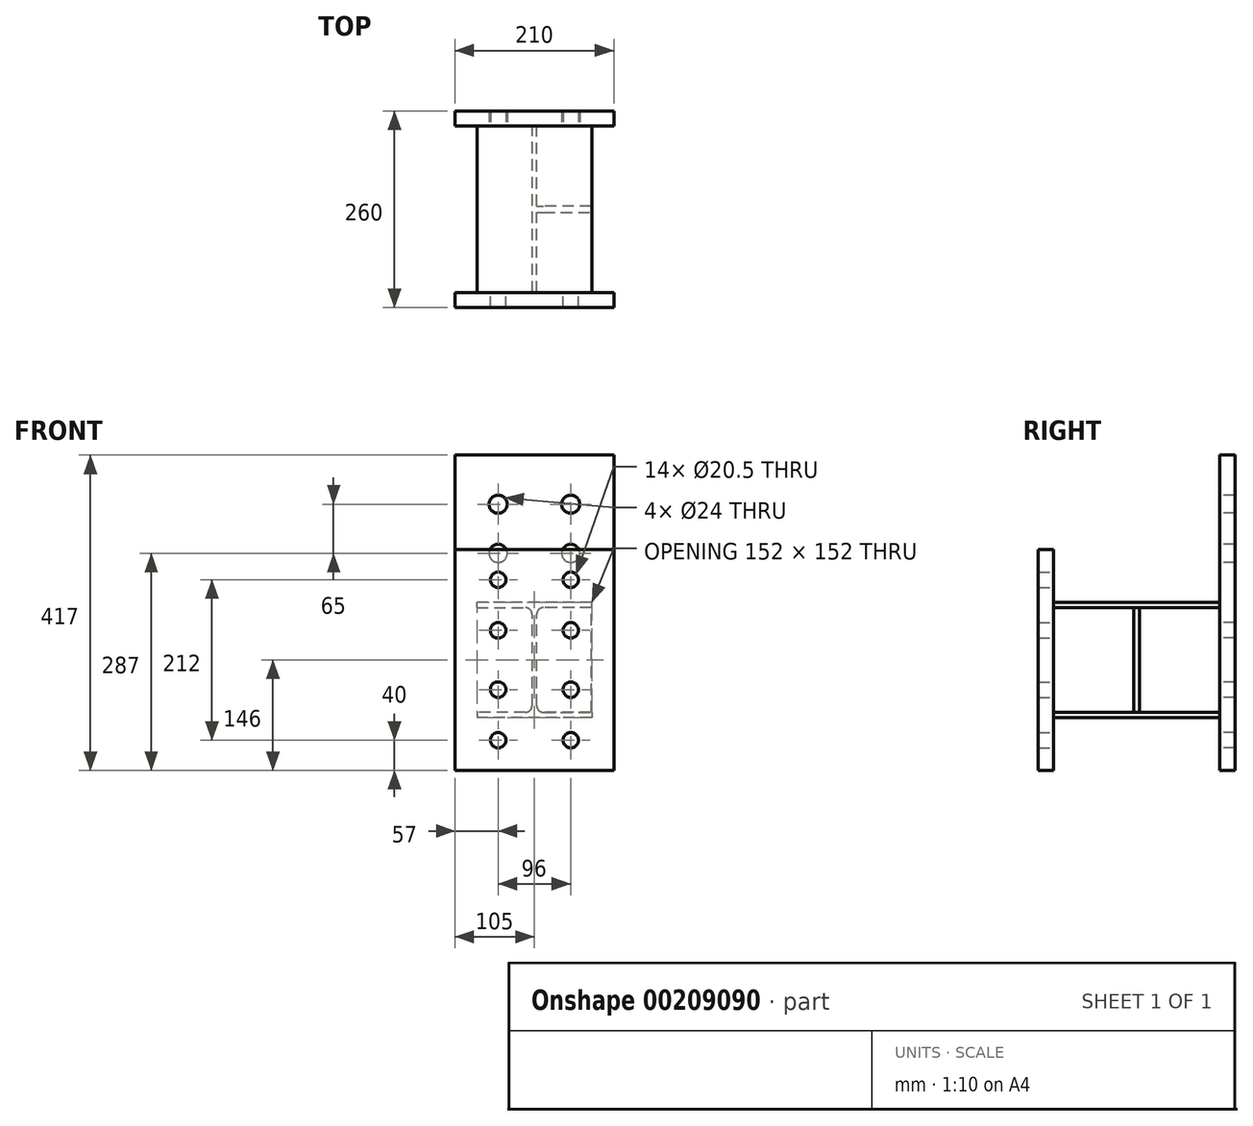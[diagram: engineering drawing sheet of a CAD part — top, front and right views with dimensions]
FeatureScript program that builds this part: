
annotation { "Feature Type Name" : "Feature", "Feature Type Description" : "" }
export const myFeature = defineFeature(function(context is Context, id is Id, definition is map)
    precondition{}
    {
        {
            var Q0;
            Q0=qCreatedBy(makeId("Front.planeOp"),FACE);
            var sketch = newSketch(context, id + "F0", { "sketchPlane" : qUnion([Q0])});
            skLineSegment(sketch, "E0.left", {"start": v(3.05, -60.3) * mm, "end": v(3.05, 60.3) * mm});
            skLineSegment(sketch, "E0.right", {"start": v(-3.05, -60.3) * mm, "end": v(-3.05, 60.3) * mm});
            skPoint(sketch, "E0.middle", {"position": v(0, 0) * mm});
            skLineSegment(sketch, "E1.bottom", {"start": v(76, 69.2) * mm, "end": v(11.95, 69.2) * mm});
            skLineSegment(sketch, "E1.top", {"start": v(76, 76) * mm, "end": v(-76, 76) * mm});
            skLineSegment(sketch, "E1.left", {"start": v(76, 69.2) * mm, "end": v(76, 76) * mm});
            skLineSegment(sketch, "E1.right", {"start": v(-76, 69.2) * mm, "end": v(-76, 76) * mm});
            skLineSegment(sketch, "E2.bottom", {"start": v(-11.95, -69.2) * mm, "end": v(-76, -69.2) * mm});
            skLineSegment(sketch, "E2.top", {"start": v(76, -76) * mm, "end": v(-76, -76) * mm});
            skLineSegment(sketch, "E2.left", {"start": v(76, -69.2) * mm, "end": v(76, -76) * mm});
            skLineSegment(sketch, "E2.right", {"start": v(-76, -69.2) * mm, "end": v(-76, -76) * mm});
            skPoint(sketch, "E3.newPointB", {"position": v(-76, 69.2) * mm});
            skArc(sketch, "E3.filletArc", {"start": v(11.95, 69.2) * mm, "mid": v(5.66, 66.6) * mm, "end": v(3.05, 60.3) * mm});
            skLineSegment(sketch, "E4", {"start": v(-76, 69.2) * mm, "end": v(-11.95, 69.2) * mm});
            skArc(sketch, "E5.filletArc", {"start": v(-3.05, 60.3) * mm, "mid": v(-5.66, 66.6) * mm, "end": v(-11.95, 69.2) * mm});
            skPoint(sketch, "E6.newPointA", {"position": v(76, -69.2) * mm});
            skArc(sketch, "E6.filletArc", {"start": v(-11.95, -69.2) * mm, "mid": v(-5.66, -66.6) * mm, "end": v(-3.05, -60.3) * mm});
            skLineSegment(sketch, "E7", {"start": v(11.95, -69.2) * mm, "end": v(76, -69.2) * mm});
            skArc(sketch, "E8.filletArc", {"start": v(3.05, -60.3) * mm, "mid": v(5.66, -66.6) * mm, "end": v(11.95, -69.2) * mm});
            skSolve(sketch);
        }
        {
            var Q0;
            Q0=qSketchRegion(id+"F0",true);
            extrude(context, id + "F1", {"entities" : qUnion([Q0]), "depth" : 220 * mm, "symmetric" : true});
        }
        {
            var Q0;
            Q0=makeQuery(id+"F1.opExtrude","SWEPT_FACE",FACE,{"disambiguationData":[OSD([sQuery(id+"F0.wireOp",EDGE,"E0.left")])]});
            var sketch = newSketch(context, id + "F2", { "sketchPlane" : qUnion([Q0])});
            skLineSegment(sketch, "E9.bottom", {"start": v(4, -69.2) * mm, "end": v(-4, -69.2) * mm});
            skLineSegment(sketch, "E9.top", {"start": v(4, 69.2) * mm, "end": v(-4, 69.2) * mm});
            skLineSegment(sketch, "E9.left", {"start": v(4, -69.2) * mm, "end": v(4, 69.2) * mm});
            skLineSegment(sketch, "E9.right", {"start": v(-4, -69.2) * mm, "end": v(-4, 69.2) * mm});
            skPoint(sketch, "E9.middle", {"position": v(0, 0) * mm});
            skSolve(sketch);
        }
        {
            var Q0;
            Q0=qSketchRegion(id+"F2",true);
            extrude(context, id + "F3", {"entities" : qUnion([Q0]), "operationType" : NewBodyOperationType.ADD, "depth" : 72 * mm});
        }
        {
            var Q0;
            Q0=makeQuery(id+"F1.opExtrude","CAP_FACE",FACE,{"disambiguationData":[OSD([sQuery(id+"F0.wireOp",EDGE,"E0.left"),sQuery(id+"F0.wireOp",EDGE,"E0.right"),sQuery(id+"F0.wireOp",EDGE,"E1.bottom"),sQuery(id+"F0.wireOp",EDGE,"E1.top"),sQuery(id+"F0.wireOp",EDGE,"E1.left"),sQuery(id+"F0.wireOp",EDGE,"E1.right"),sQuery(id+"F0.wireOp",EDGE,"E2.bottom"),sQuery(id+"F0.wireOp",EDGE,"E2.top"),sQuery(id+"F0.wireOp",EDGE,"E2.left"),sQuery(id+"F0.wireOp",EDGE,"E2.right"),sQuery(id+"F0.wireOp",EDGE,"E3.filletArc"),sQuery(id+"F0.wireOp",EDGE,"E4"),sQuery(id+"F0.wireOp",EDGE,"E5.filletArc"),sQuery(id+"F0.wireOp",EDGE,"E6.filletArc"),sQuery(id+"F0.wireOp",EDGE,"E7"),sQuery(id+"F0.wireOp",EDGE,"E8.filletArc")])],"isStart":false});
            var sketch = newSketch(context, id + "F4", { "sketchPlane" : qUnion([Q0])});
            skLineSegment(sketch, "E10.bottom", {"start": v(105, -146) * mm, "end": v(-105, -146) * mm});
            skLineSegment(sketch, "E10.top", {"start": v(105, 146) * mm, "end": v(-105, 146) * mm});
            skLineSegment(sketch, "E10.left", {"start": v(105, -146) * mm, "end": v(105, 146) * mm});
            skLineSegment(sketch, "E10.right", {"start": v(-105, -146) * mm, "end": v(-105, 146) * mm});
            skPoint(sketch, "E10.middle", {"position": v(0, 0) * mm});
            skCircle(sketch, "E11", {"center": v(-48, 106) * mm, "radius": 10.25 * mm});
            skCircle(sketch, "E12", {"center": v(-48, 39.2) * mm, "radius": 10.25 * mm});
            skCircle(sketch, "E13", {"center": v(-48, -39.2) * mm, "radius": 10.25 * mm});
            skCircle(sketch, "E14", {"center": v(-48, -106) * mm, "radius": 10.25 * mm});
            skCircle(sketch, "E15.MirrorC", {"center": v(48, -39.2) * mm, "radius": 10.25 * mm});
            skCircle(sketch, "E16.MirrorC", {"center": v(48, 39.2) * mm, "radius": 10.25 * mm});
            skCircle(sketch, "E17.MirrorC", {"center": v(48, -106) * mm, "radius": 10.25 * mm});
            skCircle(sketch, "E18.MirrorC", {"center": v(48, 106) * mm, "radius": 10.25 * mm});
            skSolve(sketch);
        }
        {
            var Q0;
            Q0=qSketchRegion(id+"F4",true);
            extrude(context, id + "F5", {"entities" : qUnion([Q0]), "operationType" : NewBodyOperationType.ADD, "depth" : 20 * mm});
        }
        {
            var Q0;
            Q0=makeQuery(id+"F1.opExtrude","CAP_FACE",FACE,{"disambiguationData":[OSD([sQuery(id+"F0.wireOp",EDGE,"E0.left"),sQuery(id+"F0.wireOp",EDGE,"E0.right"),sQuery(id+"F0.wireOp",EDGE,"E1.bottom"),sQuery(id+"F0.wireOp",EDGE,"E1.top"),sQuery(id+"F0.wireOp",EDGE,"E1.left"),sQuery(id+"F0.wireOp",EDGE,"E1.right"),sQuery(id+"F0.wireOp",EDGE,"E2.bottom"),sQuery(id+"F0.wireOp",EDGE,"E2.top"),sQuery(id+"F0.wireOp",EDGE,"E2.left"),sQuery(id+"F0.wireOp",EDGE,"E2.right"),sQuery(id+"F0.wireOp",EDGE,"E3.filletArc"),sQuery(id+"F0.wireOp",EDGE,"E4"),sQuery(id+"F0.wireOp",EDGE,"E5.filletArc"),sQuery(id+"F0.wireOp",EDGE,"E6.filletArc"),sQuery(id+"F0.wireOp",EDGE,"E7"),sQuery(id+"F0.wireOp",EDGE,"E8.filletArc")])],"isStart":true});
            var sketch = newSketch(context, id + "F6", { "sketchPlane" : qUnion([Q0])});
            skLineSegment(sketch, "E19.bottom", {"start": v(-105, -146) * mm, "end": v(105, -146) * mm});
            skLineSegment(sketch, "E19.top", {"start": v(-105, 271) * mm, "end": v(105, 271) * mm});
            skLineSegment(sketch, "E19.left", {"start": v(-105, -146) * mm, "end": v(-105, 271) * mm});
            skLineSegment(sketch, "E19.right", {"start": v(105, 271) * mm, "end": v(105, -146) * mm});
            skCircle(sketch, "E20", {"center": v(-48, 39.2) * mm, "radius": 10.25 * mm});
            skCircle(sketch, "E21.MirrorC", {"center": v(-48, -106) * mm, "radius": 10.25 * mm});
            skCircle(sketch, "E22.MirrorC", {"center": v(-48, -39.2) * mm, "radius": 10.25 * mm});
            skLineSegment(sketch, "E23", {"start": v(0, 0) * mm, "end": v(0, 68.37) * mm});
            skPoint(sketch, "E23.endSnap0", {"position": v(0, 76) * mm});
            skCircle(sketch, "E24.MirrorC", {"center": v(48, -106) * mm, "radius": 10.25 * mm});
            skCircle(sketch, "E25.MirrorC", {"center": v(48, -39.2) * mm, "radius": 10.25 * mm});
            skCircle(sketch, "E26.MirrorC", {"center": v(48, 39.2) * mm, "radius": 10.25 * mm});
            skCircle(sketch, "E27", {"center": v(-48, 141) * mm, "radius": 12 * mm});
            skCircle(sketch, "E28", {"center": v(-48, 206) * mm, "radius": 12 * mm});
            skCircle(sketch, "E29.MirrorC", {"center": v(48, 141) * mm, "radius": 12 * mm});
            skCircle(sketch, "E30.MirrorC", {"center": v(48, 206) * mm, "radius": 12 * mm});
            skSolve(sketch);
        }
        {
            var Q0;
            Q0=qSketchRegion(id+"F6",true);
            extrude(context, id + "F7", {"entities" : qUnion([Q0]), "operationType" : NewBodyOperationType.ADD, "depth" : 20 * mm});
        }
    });
